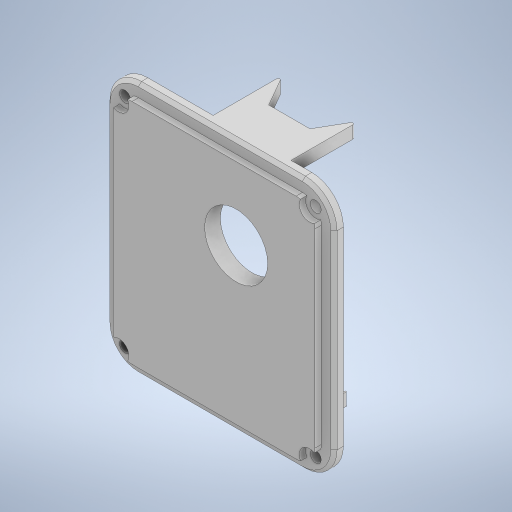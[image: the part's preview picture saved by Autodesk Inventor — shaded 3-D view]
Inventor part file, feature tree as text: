
AUTODESK INVENTOR PART (.ipt)
format: ipt  version: 2023 (Build 270158000, 158)  size: 412,160 bytes
history: native  units: mm
features: extrude x9, sketch x7, projected_geometry x3, fillet x2, other x1, chamfer x1
ambient origin geometry x8: Origin, YZ Plane, XZ Plane, XY Plane, X Axis, Y Axis, Z Axis, Center Point
bodies: Body1 (feature_tree)
feature tree (23):
  other  "솔리드1"
  sketch  "스케치1"
  extrude  "돌출1"  Depth=72.0mm
  extrude  "돌출2"  Depth=80.2mm
  extrude  "돌출3"  Depth=10.0mm
  extrude  "돌출5"  Depth=4.0mm
  fillet  "모깎기1"  Radius=3.5mm
  extrude  "돌출6"  Depth=6.5mm
  extrude  "돌출7"  Depth=3.0mm TaperAngle=0.0deg
  fillet  "모깎기2"  Radius=41.3mm
  extrude  "돌출8"  Depth=2.0mm TaperAngle=0.0deg
  chamfer  "모따기1"  Distance=10.0mm
  extrude  "돌출10"  Depth=27.0mm TaperAngle=0.0deg
  extrude  "돌출11"  Depth=25.0mm
  sketch  "스케치10"
  sketch  "스케치3"
  projected_geometry  "투영된 루프1"
  sketch  "스케치5"
  sketch  "스케치6"
  sketch  "스케치8"
  sketch  "스케치9"
  projected_geometry  "투영된 루프3"
  projected_geometry  "투영된 루프4"
